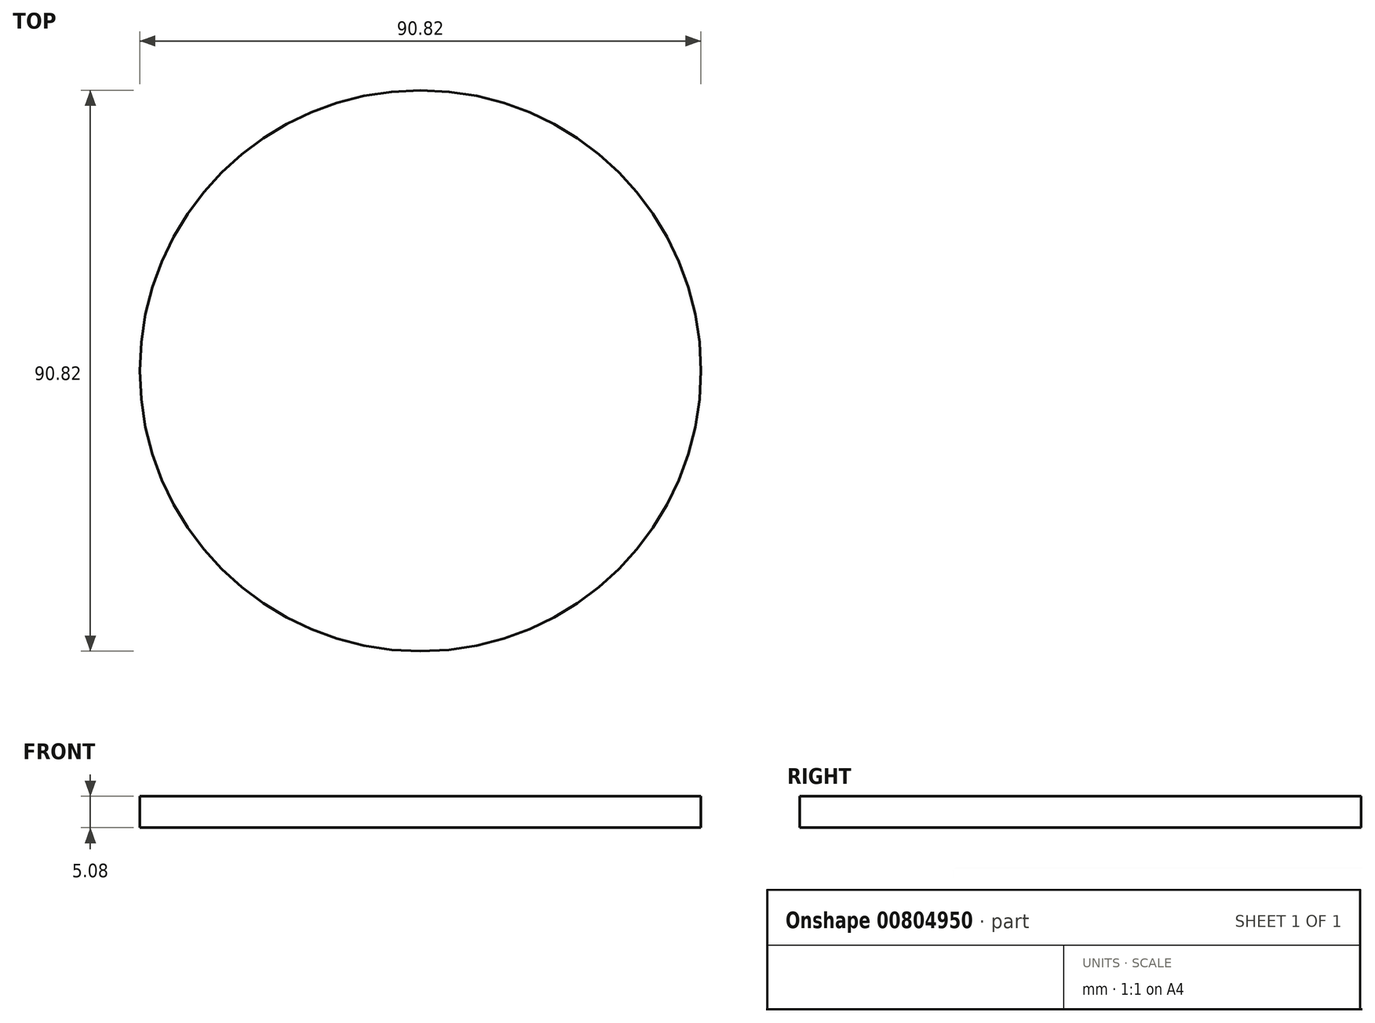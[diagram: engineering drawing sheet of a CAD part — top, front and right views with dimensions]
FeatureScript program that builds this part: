
annotation { "Feature Type Name" : "Feature", "Feature Type Description" : "" }
export const myFeature = defineFeature(function(context is Context, id is Id, definition is map)
    precondition{}
    {
        {
            var Q0;
            Q0=qCreatedBy(makeId("Top.planeOp"),FACE);
            var sketch = newSketch(context, id + "F0", { "sketchPlane" : qUnion([Q0])});
            skCircle(sketch, "E0", {"center": v(0, 0) * mm, "radius": 45.41 * mm});
            skSolve(sketch);
        }
        {
            var Q0;
            Q0=makeQuery(id+"F0.imprint","IMPRINT",FACE,{"disambiguationData":[TD([[makeQuery(id+"F0.imprint","IMPRINT",EDGE,{"derivedFrom":sQuery(id+"F0.wireOp",EDGE,"E0")}),1.0]])]});
            extrude(context, id + "F1", {"entities" : qUnion([Q0]), "depth" : 5.08 * mm, "offsetDistance" : 25.4 * mm});
        }
    });
